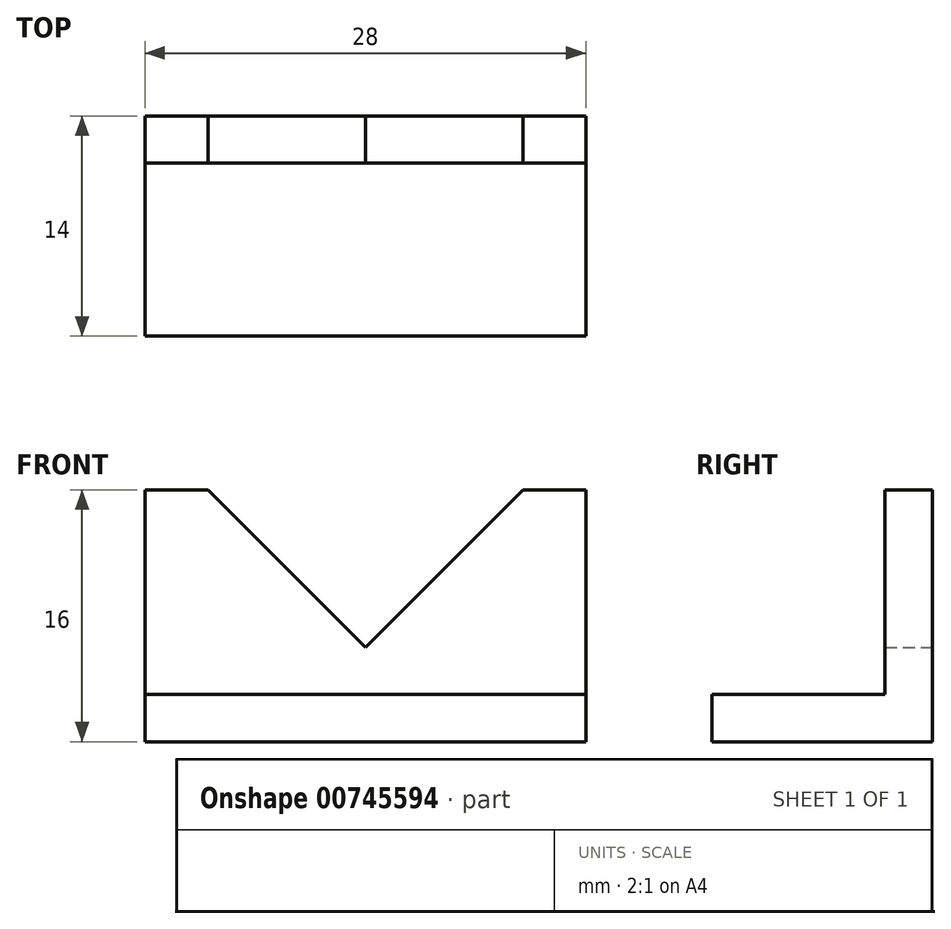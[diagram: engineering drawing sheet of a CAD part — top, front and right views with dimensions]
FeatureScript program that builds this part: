
annotation { "Feature Type Name" : "Feature", "Feature Type Description" : "" }
export const myFeature = defineFeature(function(context is Context, id is Id, definition is map)
    precondition{}
    {
        {
            var Q0;
            Q0=qCreatedBy(makeId("Front.planeOp"),FACE);
            var sketch = newSketch(context, id + "F0", { "sketchPlane" : qUnion([Q0])});
            skLineSegment(sketch, "E0", {"start": v(-14, 16) * mm, "end": v(-14, 0) * mm});
            skLineSegment(sketch, "E1", {"start": v(-14, 0) * mm, "end": v(14, 0) * mm});
            skLineSegment(sketch, "E2", {"start": v(14, 0) * mm, "end": v(14, 16) * mm});
            skLineSegment(sketch, "E3", {"start": v(14, 16) * mm, "end": v(10, 16) * mm});
            skLineSegment(sketch, "E4", {"start": v(10, 16) * mm, "end": v(0, 6) * mm});
            skLineSegment(sketch, "E5", {"start": v(0, 6) * mm, "end": v(-10, 16) * mm});
            skLineSegment(sketch, "E6", {"start": v(-10, 16) * mm, "end": v(-14, 16) * mm});
            skSolve(sketch);
        }
        {
            var Q0;
            Q0 = qSketchRegion(id + "F0", true);
            extrude(context, id + "F1", {"entities" : qUnion([Q0]), "depth" : 3 * mm, "offsetDistance" : 25 * mm});
        }
        {
            var Q0;
            Q0=makeQuery(id+"F1.opExtrude","CAP_FACE",FACE,{"disambiguationData":[OSD([sQuery(id+"F0.wireOp",EDGE,"E0"),sQuery(id+"F0.wireOp",EDGE,"E1"),sQuery(id+"F0.wireOp",EDGE,"E2"),sQuery(id+"F0.wireOp",EDGE,"E3"),sQuery(id+"F0.wireOp",EDGE,"E4"),sQuery(id+"F0.wireOp",EDGE,"E5"),sQuery(id+"F0.wireOp",EDGE,"E6")])],"isStart":false});
            var sketch = newSketch(context, id + "F2", { "sketchPlane" : qUnion([Q0])});
            skLineSegment(sketch, "E7.bottom", {"start": v(-14, 0) * mm, "end": v(14, 0) * mm});
            skLineSegment(sketch, "E7.top", {"start": v(-14, 3) * mm, "end": v(14, 3) * mm});
            skLineSegment(sketch, "E7.left", {"start": v(-14, 0) * mm, "end": v(-14, 3) * mm});
            skLineSegment(sketch, "E7.right", {"start": v(14, 0) * mm, "end": v(14, 3) * mm});
            skSolve(sketch);
        }
        {
            var Q0;
            Q0 = qSketchRegion(id + "F2", true);
            extrude(context, id + "F3", {"entities" : qUnion([Q0]), "operationType" : NewBodyOperationType.ADD, "depth" : (14 - 3) * mm, "offsetDistance" : 25 * mm});
        }
    });
